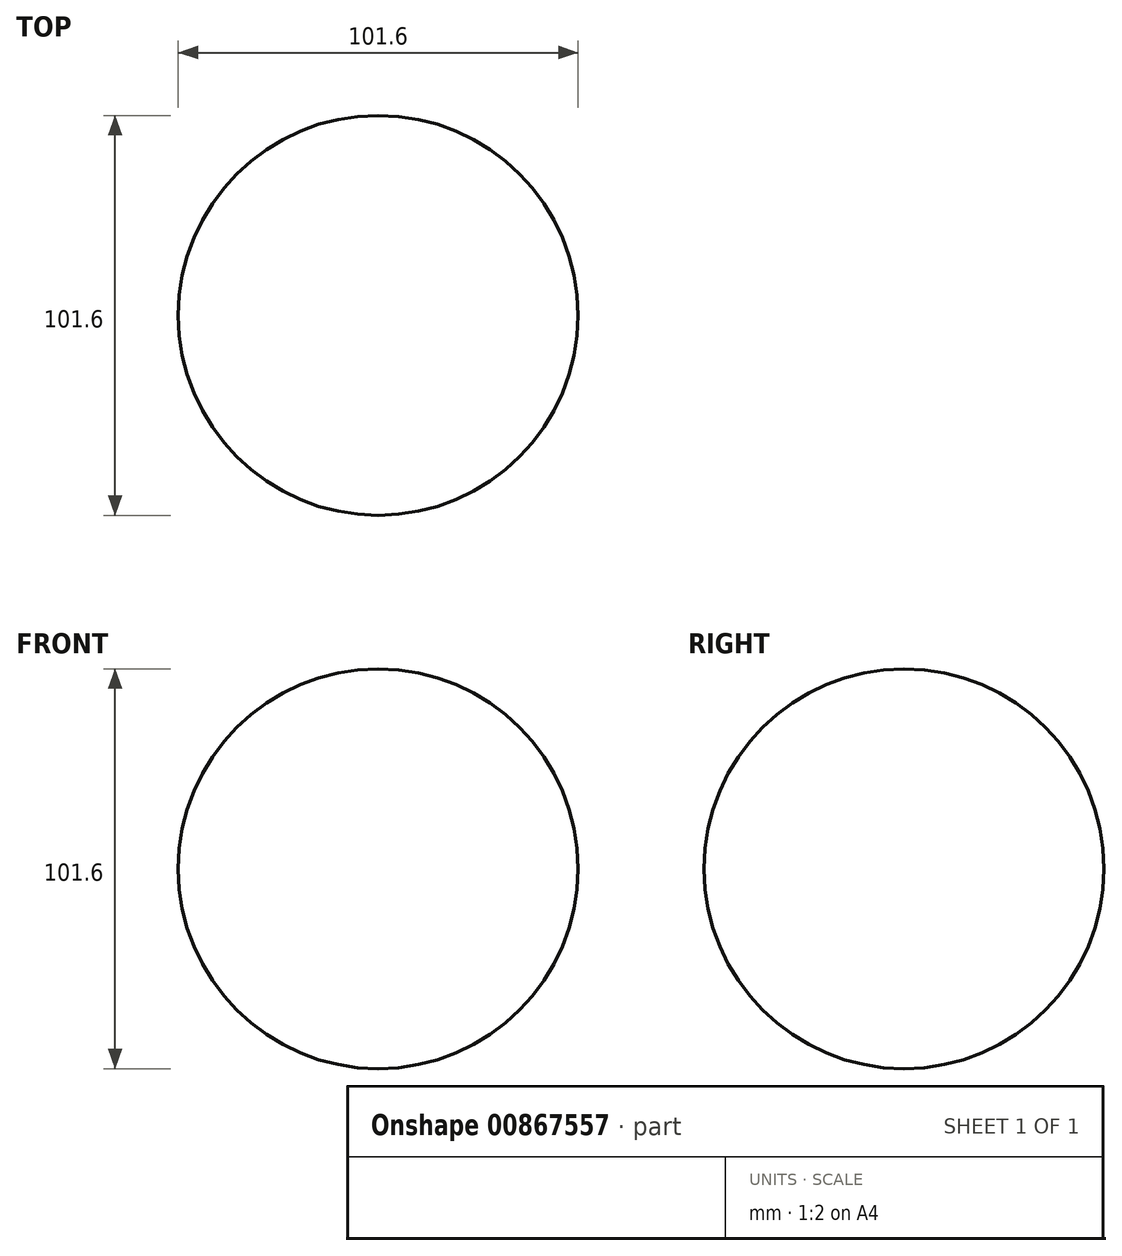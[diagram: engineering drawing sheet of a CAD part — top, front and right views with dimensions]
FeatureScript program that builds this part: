
annotation { "Feature Type Name" : "Feature", "Feature Type Description" : "" }
export const myFeature = defineFeature(function(context is Context, id is Id, definition is map)
    precondition{}
    {
        {
            var Q0;
            Q0=qCreatedBy(makeId("Front.planeOp"),FACE);
            var sketch = newSketch(context, id + "F0", { "sketchPlane" : qUnion([Q0])});
            skArc(sketch, "E0", {"start": v(0, -50.8) * mm, "mid": v(50.8, 0) * mm, "end": v(0, 50.8) * mm});
            skLineSegment(sketch, "E1", {"start": v(0, 50.8) * mm, "end": v(0, -50.8) * mm});
            skSolve(sketch);
        }
        {
            var Q0;
            Q0=makeQuery(id+"F0.imprint","IMPRINT",FACE,{"disambiguationData":[TD([[makeQuery(id+"F0.imprint","IMPRINT",EDGE,{"derivedFrom":sQuery(id+"F0.wireOp",EDGE,"E0")}),1.0]])]});
            var Q1;
            Q1=sQuery(id+"F0.wireOp",EDGE,"E1");
            revolve(context, id + "F1", {"surfaceOperationType" : NewSurfaceOperationType.NEW, "entities" : qUnion([Q0]), "axis" : qUnion([Q1]), "revolveType" : RevolveType.FULL});
        }
    });
